# Revit family: MG MOJAVE
name_source: partatom
category: Plumbing Fixtures
units: mm (PartAtom-declared; Revit-internal decimal feet)

## family parameters
Always vertical = Yes
Cut with Voids When Loaded = No
OmniClass Number = 23.45.00.00
OmniClass Title = Sanitary, Laundry, and Cleaning Equipment
Part Type = Normal
Room Calculation Point = No
Round Connector Dimension = Use Diameter
Shared = No
Work Plane-Based = No

## types (2) — shared parameters
CW Connection = Yes
Default Elevation = 0"
High Gloss Ceramic = High Gloss Ceramic
Inlet Threads = Feeding: ¾" (19 mm) Flush: 2" 11 - ½ NPT
Manufacturer = HELVEX
Max. Working Pressure = 85.3 psi
Min. Working Pressure = 14.2 psi
Total Width = 14"
Type Comments = SANIVEX

## per-type parameters (varying)
| type | Certification | Data Sheet | Description | Features | Instructive | Model | Note | Total Height | Total Length | Type Image | URL |
| MG FERRY | http://www.helvex.com.mx | http://www.helvex.com.mx | Travis Flush Washout Urinal | Hydraulic Seal, Includes Gasket And Spud; Includes Two Settings Kits; Includes Stainless Steel Drain; Water Saving; Requires 0.26 gpf Or 0.13 gpf | http://www.helvex.com.mx | MG-2 | CNCP Certified | 26" | 19" | <None> | http://www.helvex.com.mx |
| MG MOJAVE | https://www.helvex.com.mx | https://www.helvex.com.mx | Mingitorio tipo Cascada para Flux | Mingitorio tipo cascada para flux..metro 0,5 lpd .. 1 lpd con
completo intercambio de agua en el sello hidra..lico de
28mm. | https://www.helvex.com.mx | MG MOJAVE | https://www.helvex.com.mx | 23" | 12" | MG MOJAVE.jpg | https://www.helvex.com.mx |

## geometry (parser evidence)
native form markers: Sweep x3
no freeform markers — native parametric forms only
